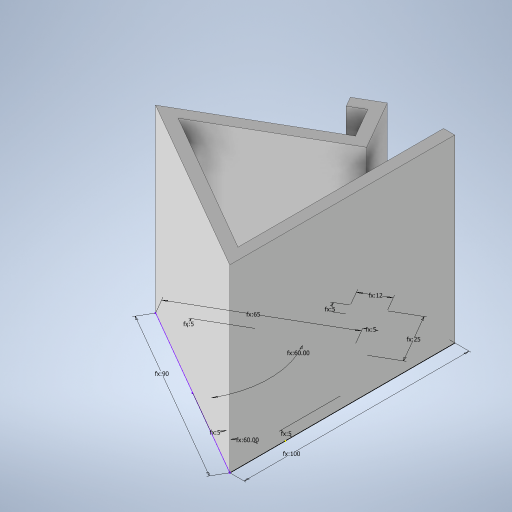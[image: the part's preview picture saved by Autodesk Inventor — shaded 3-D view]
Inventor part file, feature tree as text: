
AUTODESK INVENTOR PART (.ipt)
format: ipt  version: 2024.2 (Build 282272000, 272)  size: 264,704 bytes
history: native  units: in
note: dims shown in document units (in); Inventor stores cm internally (conversion verified against a paired STEP export)
features: extrude x2, other x2
ambient origin geometry x8: Origin, YZ Plane, XZ Plane, XY Plane, X Axis, Y Axis, Z Axis, Center Point
bodies: Solid1 (feature_tree)
feature tree (4):
  extrude  "MainBody"  TaperAngle=0.0deg  [1 undecoded]
  extrude  "CentralNotch"  Depth=3.1496in
  other  "PhoneStandProfile"
  other  "Rectangle"
note: 1 required parameter value undecoded (feature->parameter linkage not recoverable at this tier; creation-order binding heuristic only, values carry confidence <= 0.55)
